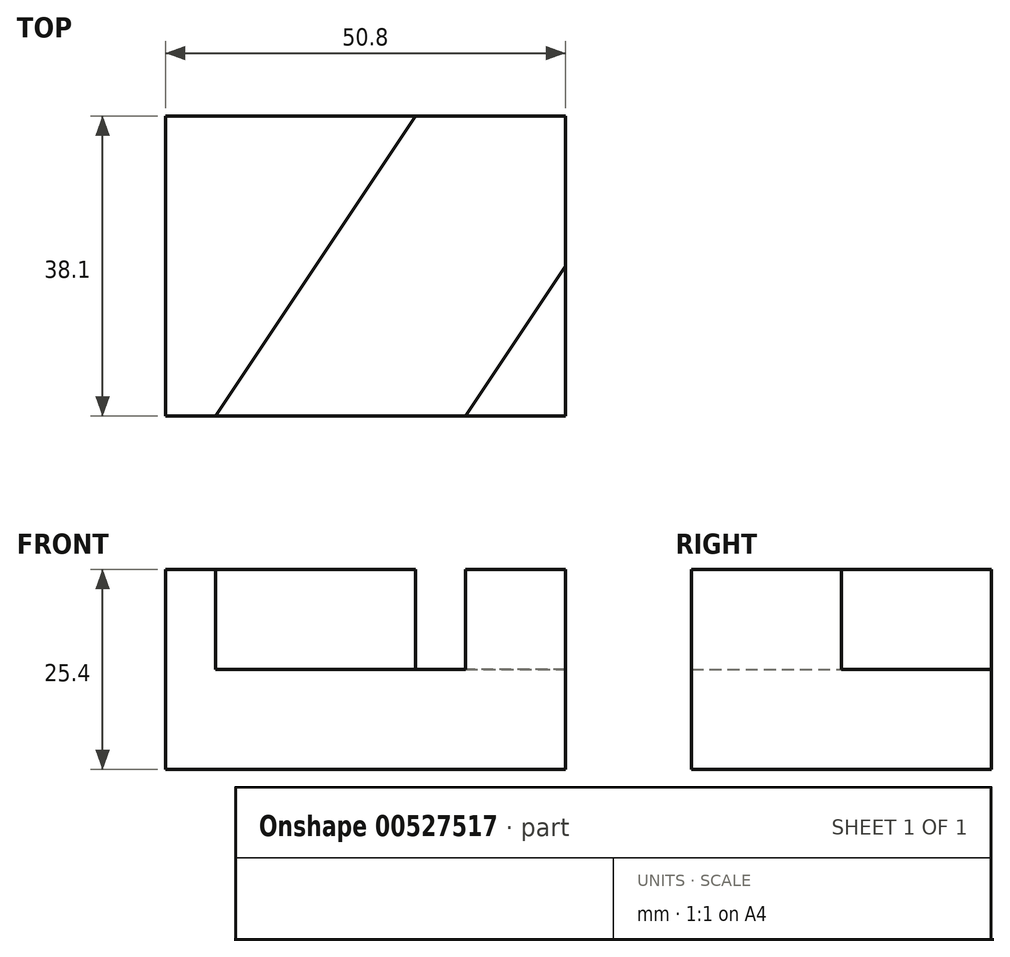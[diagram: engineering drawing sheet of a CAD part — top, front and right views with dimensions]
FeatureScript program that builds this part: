
annotation { "Feature Type Name" : "Feature", "Feature Type Description" : "" }
export const myFeature = defineFeature(function(context is Context, id is Id, definition is map)
    precondition{}
    {
        {
            var Q0;
            Q0=qCreatedBy(makeId("Front.planeOp"),FACE);
            var sketch = newSketch(context, id + "F0", { "sketchPlane" : qUnion([Q0])});
            skLineSegment(sketch, "E0", {"start": v(0, 0) * mm, "end": v(50.8, 0) * mm});
            skLineSegment(sketch, "E1", {"start": v(50.8, 0) * mm, "end": v(50.8, 25.4) * mm});
            skLineSegment(sketch, "E2", {"start": v(50.8, 25.4) * mm, "end": v(0, 25.4) * mm});
            skLineSegment(sketch, "E3", {"start": v(0, 25.4) * mm, "end": v(0, 0) * mm});
            skSolve(sketch);
        }
        {
            var Q0;
            Q0=makeQuery(id+"F0.imprint","IMPRINT",FACE,{"disambiguationData":[TD([[makeQuery(id+"F0.imprint","IMPRINT",EDGE,{"derivedFrom":sQuery(id+"F0.wireOp",EDGE,"E0")}),1.0]])]});
            extrude(context, id + "F1", {"entities" : qUnion([Q0]), "oppositeDirection" : true, "depth" : 38.1 * mm, "offsetDistance" : 25.4 * mm});
        }
        {
            var Q0;
            Q0=makeQuery(id+"F1.opExtrude","SWEPT_FACE",FACE,{"disambiguationData":[OSD([sQuery(id+"F0.wireOp",EDGE,"E2")])]});
            var sketch = newSketch(context, id + "F2", { "sketchPlane" : qUnion([Q0])});
            skLineSegment(sketch, "E4", {"start": v(0, 0) * mm, "end": v(6.35, 0) * mm});
            skLineSegment(sketch, "E5", {"start": v(6.35, 0) * mm, "end": v(31.75, 38.1) * mm});
            skLineSegment(sketch, "E6", {"start": v(31.75, 38.1) * mm, "end": v(0, 38.1) * mm});
            skLineSegment(sketch, "E7", {"start": v(0, 38.1) * mm, "end": v(0, 0) * mm});
            skLineSegment(sketch, "E8", {"start": v(31.75, 38.1) * mm, "end": v(50.8, 38.1) * mm});
            skLineSegment(sketch, "E9", {"start": v(50.8, 0) * mm, "end": v(38.1, 0) * mm});
            skLineSegment(sketch, "E10", {"start": v(38.1, 0) * mm, "end": v(50.8, 19.05) * mm});
            skLineSegment(sketch, "E11", {"start": v(50.8, 19.05) * mm, "end": v(50.8, 0) * mm});
            skLineSegment(sketch, "E12", {"start": v(50.8, 19.05) * mm, "end": v(50.8, 38.1) * mm});
            skSolve(sketch);
        }
        {
            var Q0;
            {var subQ1=sQuery(id+"F2.wireOp",EDGE,"E5");Q0=makeQuery(id+"F2.imprint","IMPRINT",FACE,{"disambiguationData":[TD([[makeQuery(id+"F2.imprint","IMPRINT",EDGE,{"derivedFrom":subQ1}),-1.0]])]});}
            extrude(context, id + "F3", {"entities" : qUnion([Q0]), "operationType" : NewBodyOperationType.REMOVE, "oppositeDirection" : true, "depth" : 12.7 * mm, "offsetDistance" : 25.4 * mm});
        }
    });
